# Revit family: Haworth_Lively_Chair_Task_EU_PRELIMINARY
name_source: partatom
category: Furniture
units: mm (PartAtom-declared; Revit-internal decimal feet)

## family parameters
Always vertical = Yes
Cut with Voids When Loaded = No
OmniClass Number = 23.40.70.14.64.11
OmniClass Title = Office Furniture
Room Calculation Point = No
Shared = No
Work Plane-Based = No

## types (4) — shared parameters
Adjustable Lumbar = Yes
Arm Finish = Haworth - Plastic - Black
Assembly Code = E2020200
Caster Finish = Haworth - Plastic - Black
Description = Haworth - Lively - Chair - Task
Manufacturer = Haworth
Model = 29X0
Product URL = https://www.haworth.com
Revision Number = 1
Size = Verify Final Dim. w/ Haworth
URL = https://www.haworth.com
Warranty = http://www.haworth.com

## per-type parameters (varying)
| type | Adjustable Arms | Casters | Glides | Mesh Back | Upholstered Back | Without Arms |
| Adjustable Arms - Mesh Back | Yes | No | Yes | Yes | No | No |
| Without Arms - Mesh Back | No | No | Yes | Yes | No | Yes |
| Adjustable Arms - Upholstered Back | Yes | Yes | No | No | Yes | No |
| Without Arms - Upholstered Back | No | Yes | No | No | Yes | Yes |

## geometry (parser evidence)
native form markers: Blend x30, Sweep x13
no freeform markers — native parametric forms only
